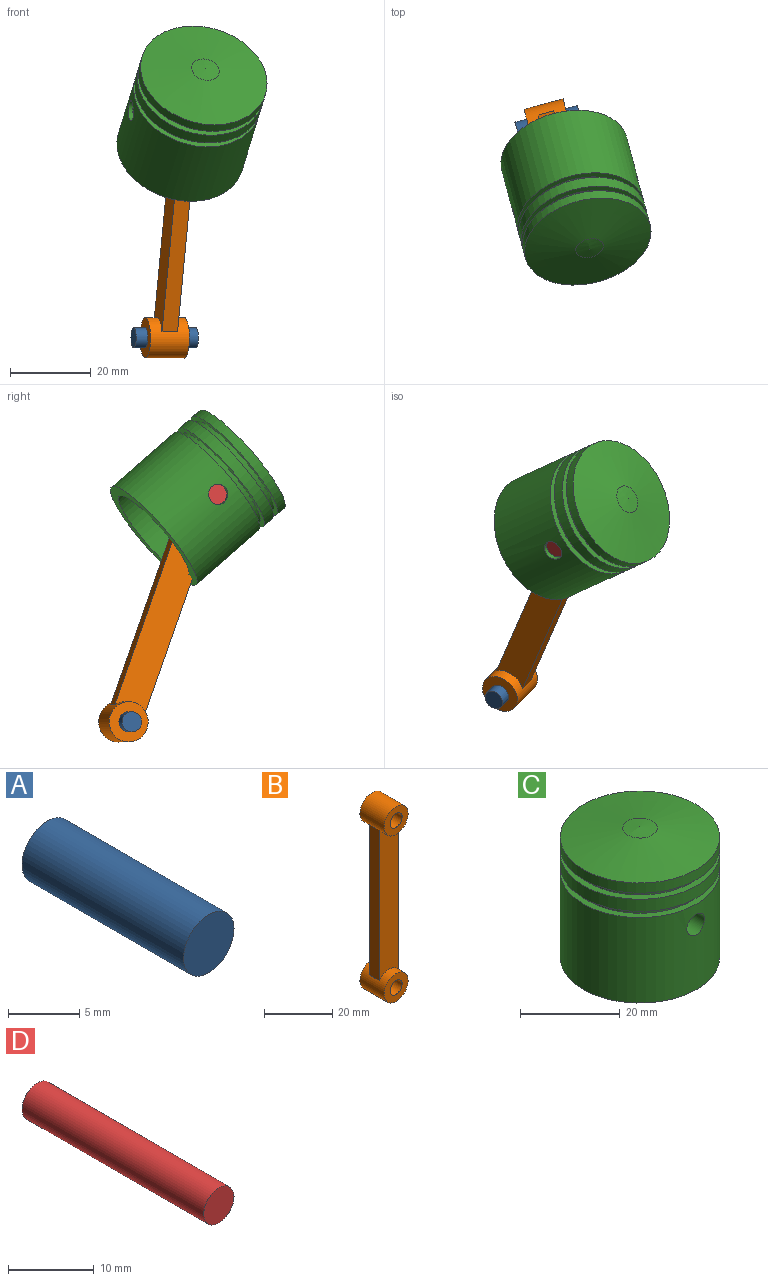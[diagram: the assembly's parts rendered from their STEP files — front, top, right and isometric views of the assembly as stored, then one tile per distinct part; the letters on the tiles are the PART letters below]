
ASSEMBLY  parts=4 mates=3
PART A: 3 faces, bbox 5x16x5 mm
  f0: cylinder r=2.5mm len=16mm, axis (0,1,0), area 251.3mm2, adj f1,f2
  f1: plane 5x5mm, normal (0,-1,0), area 19.6mm2, adj f0
  f2: plane 5x5mm, normal (0,1,0), area 19.6mm2, adj f0
PART B: 12 faces, bbox 10x10x70 mm
  f0: plane 54x8mm, normal (0,-1,0), area 409.6mm2, adj f2,f3,f4,f5
  f1: plane 54x8mm, normal (0,1,0), area 409.6mm2, adj f2,f3,f4,f5
  f2: cylinder r=5mm len=10mm, axis (0,1,0), area 277.1mm2, adj f0,f1,f3,f5,f8,f9
  f3: plane 54x4mm, normal (-1,0,0), area 216mm2, adj f0,f1,f2,f4
  f4: cylinder r=5mm len=10mm, axis (0,1,0), area 277.1mm2, adj f0,f1,f3,f5,f6,f7
  f5: plane 54x4mm, normal (1,0,0), area 216mm2, adj f0,f1,f2,f4
  f6: plane 10x10mm, normal (0,1,0), area 58.9mm2, adj f4,f11
  f7: plane 10x10mm, normal (0,-1,0), area 58.9mm2, adj f4,f11
  f8: plane 10x10mm, normal (0,1,0), area 58.9mm2, adj f2,f10
  f9: plane 10x10mm, normal (0,-1,0), area 58.9mm2, adj f2,f10
  f10: cylinder r=2.5mm len=10mm, axis (0,-1,0), area 157.1mm2, adj f8,f9
  f11: cylinder r=2.5mm len=10mm, axis (0,-1,0), area 157.1mm2, adj f6,f7
PART C: 18 faces, bbox 32x32x32 mm
  f0: cylinder r=10mm len=20mm, axis (0,0,-1), area 588.7mm2, adj f1,f14,f15,f16
  f1: cylinder r=2.5mm len=6.32mm, axis (0,-1,0), area 95.2mm2, adj f0,f9
  f2: plane 32x32mm, normal (0,0,1), area 143.7mm2, adj f3,f13
  f3: cylinder r=14.5mm len=29mm, axis (0,0,-1), area 136.7mm2, adj f2,f4
  f4: plane 32x32mm, normal (0,0,-1), area 143.7mm2, adj f3,f5
  f5: cylinder r=16mm len=32mm, axis (0,0,-1), area 250.1mm2, adj f4,f6
  f6: cone r=3.47mm half-angle=80deg, axis (0,0,-1), area 778.2mm2, adj f5,f7
  f7: sphere r=20mm, area 38.2mm2, adj f6
  f8: plane 32x32mm, normal (0,0,-1), area 273.3mm2, adj f9,f17
  f9: cylinder r=16mm len=32mm, axis (0,0,-1), area 2071.6mm2, adj f1,f8,f10,f14
  f10: plane 32x32mm, normal (0,0,1), area 143.7mm2, adj f9,f11
  f11: cylinder r=14.5mm len=29mm, axis (0,0,-1), area 136.7mm2, adj f10,f12
  f12: plane 32x32mm, normal (0,0,-1), area 143.7mm2, adj f11,f13
  f13: cylinder r=16mm len=32mm, axis (0,0,-1), area 301.6mm2, adj f2,f12
  f14: cylinder r=2.5mm len=6.32mm, axis (0,-1,0), area 95.2mm2, adj f0,f9
  f15: plane 20x20mm, normal (0,0,-1), area 314.2mm2, adj f0
  f16: plane 26x26mm, normal (0,0,-1), area 216.8mm2, adj f0,f17
  f17: cylinder r=13mm len=26mm, axis (0,0,-1), area 816.8mm2, adj f8,f16
PART D: 3 faces, bbox 5x30x5 mm
  f0: cylinder r=2.5mm len=30mm, axis (0,1,0), area 471.2mm2, adj f1,f2
  f1: plane 5x5mm, normal (0,-1,0), area 19.6mm2, adj f0
  f2: plane 5x5mm, normal (0,1,0), area 19.6mm2, adj f0
PLACE A rot(axis=(0.17,0.22,-0.96),77.2deg) t=(-45.5,51.5,-67.79)mm
PLACE B rot(axis=(0.17,0.22,-0.96),77.2deg) t=(-34.15,9.14,-59.4)mm
PLACE C rot(axis=(0.37,0.48,-0.79),88.1deg) t=(-41.54,43.46,-39.22)mm
PLACE D rot(axis=(0.37,0.48,-0.79),88.1deg) t=(-48.43,70.17,23.72)mm
MATE fastened D.f0 <-> C.f1  axis (-0.97,-0.26,0) through (-39.98,-19.33,12.02)mm
MATE fastened B.f4 <-> A.f0  axis (0.97,0.26,0) through (-32.73,3.85,-44.36)mm
MATE cylindrical B.f2 <-> D.f0  axis (0.97,0.26,0) through (-27.42,-15.97,12.02)mm
